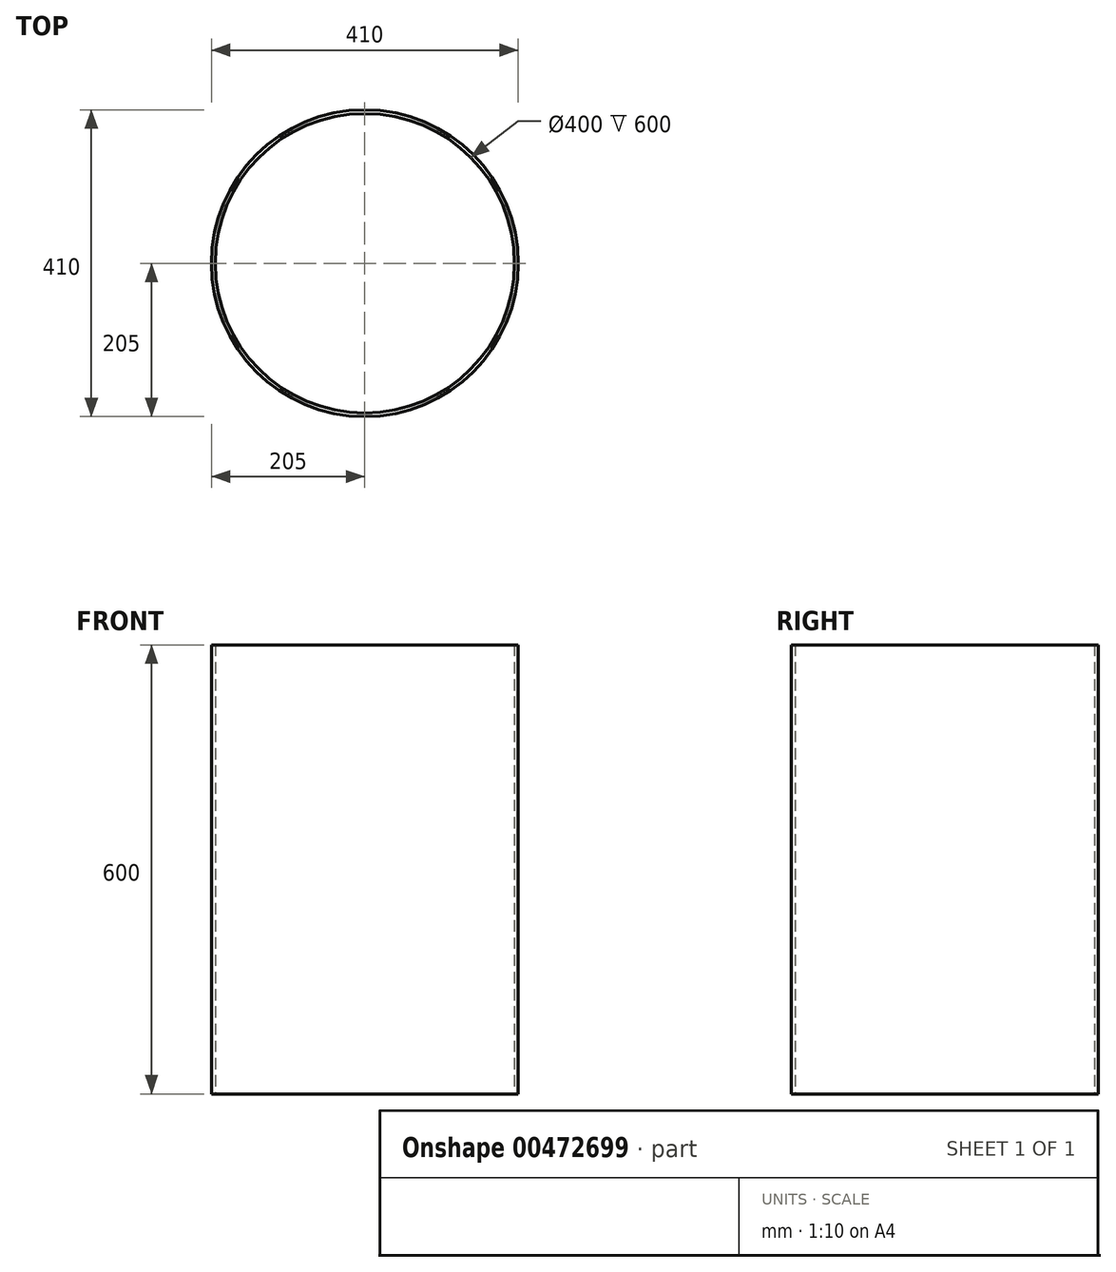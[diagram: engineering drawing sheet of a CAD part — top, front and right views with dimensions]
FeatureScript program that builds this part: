
annotation { "Feature Type Name" : "Feature", "Feature Type Description" : "" }
export const myFeature = defineFeature(function(context is Context, id is Id, definition is map)
    precondition{}
    {
        {
            var Q0;
            Q0=qCreatedBy(makeId("Top.planeOp"),FACE);
            var sketch = newSketch(context, id + "F0", { "sketchPlane" : qUnion([Q0])});
            skCircle(sketch, "E0", {"center": v(0, 0) * mm, "radius": 200 * mm});
            skCircle(sketch, "E1", {"center": v(0, 0) * mm, "radius": 205 * mm});
            skSolve(sketch);
        }
        {
            var Q0;
            Q0 = qSketchRegion(id + "F0", true);
            extrude(context, id + "F1", {"entities" : qUnion([Q0]), "depth" : 600 * mm});
        }
    });
